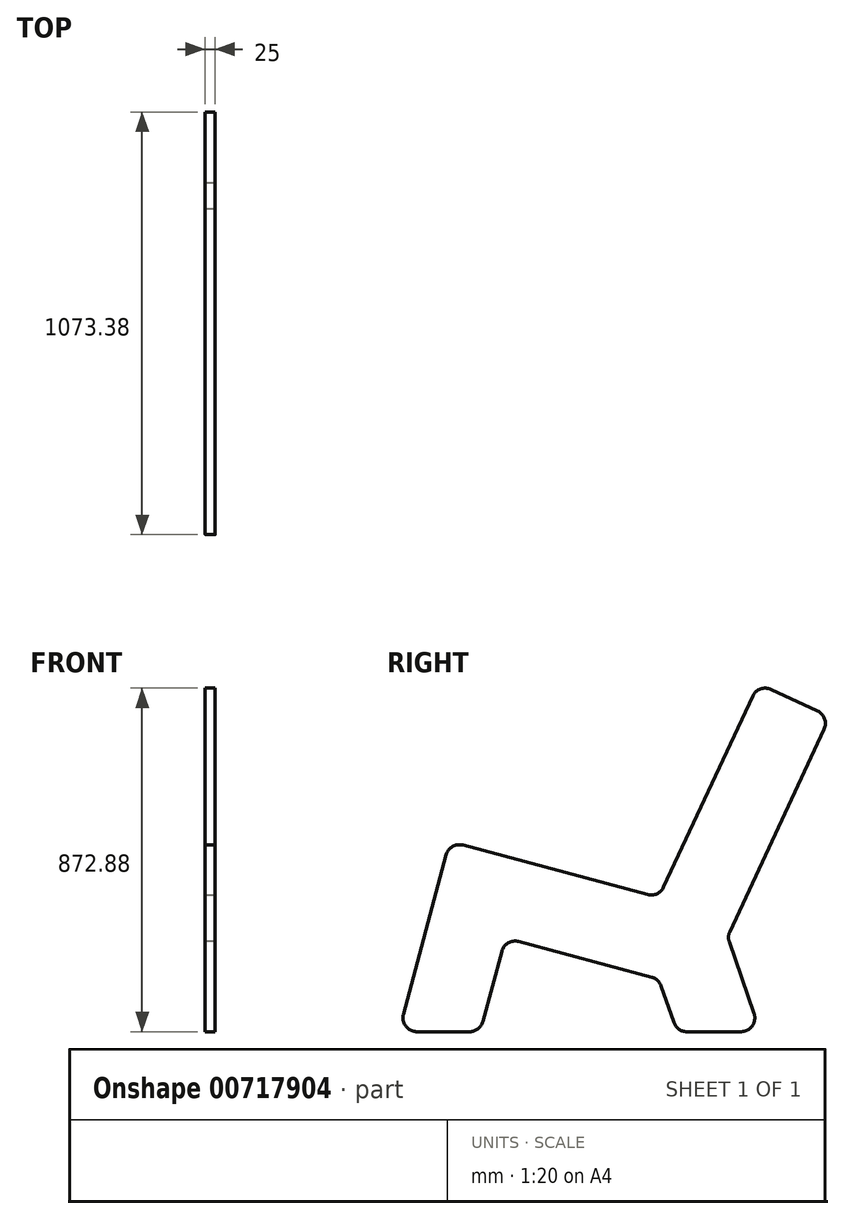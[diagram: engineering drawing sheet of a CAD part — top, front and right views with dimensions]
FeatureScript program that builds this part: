
annotation { "Feature Type Name" : "Feature", "Feature Type Description" : "" }
export const myFeature = defineFeature(function(context is Context, id is Id, definition is map)
    precondition{}
    {
        {
            var Q0;
            Q0=qCreatedBy(makeId("Right.planeOp"),FACE);
            cPlane(context, id + "F0", {"entities" : qUnion([Q0]), "cplaneType" : CPlaneType.OFFSET, "offset" : 400 * mm, "oppositeDirection" : true, "width" : 150 * mm, "height" : 150 * mm});
        }
        {
            var Q0;
            Q0=qCreatedBy(id+"F0.planeOp",FACE);
            var sketch = newSketch(context, id + "F1", { "sketchPlane" : qUnion([Q0])});
            skLineSegment(sketch, "E0", {"start": v(0, 0) * mm, "end": v(129.4, 482.96) * mm});
            skLineSegment(sketch, "E1", {"start": v(129.4, 482.96) * mm, "end": v(660.67, 340.61) * mm});
            skLineSegment(sketch, "E2", {"start": v(660.67, 340.61) * mm, "end": v(914.24, 884.4) * mm});
            skLineSegment(sketch, "E3", {"start": v(914.24, 884.4) * mm, "end": v(1095.5, 799.87) * mm});
            skLineSegment(sketch, "E4.0", {"start": v(207.06, 0) * mm, "end": v(270.83, 238.01) * mm});
            skLineSegment(sketch, "E5.0", {"start": v(270.83, 238.01) * mm, "end": v(660.67, 133.56) * mm});
            skLineSegment(sketch, "E6", {"start": v(0, 0) * mm, "end": v(207.06, 0) * mm});
            skLineSegment(sketch, "E7.0", {"start": v(835, 241.22) * mm, "end": v(1095.5, 799.87) * mm});
            skLineSegment(sketch, "E8", {"start": v(660.67, 133.56) * mm, "end": v(707.06, 0) * mm});
            skLineSegment(sketch, "E9.0", {"start": v(835, 241.22) * mm, "end": v(918.77, 0) * mm});
            skLineSegment(sketch, "E10", {"start": v(707.06, 0) * mm, "end": v(918.77, 0) * mm});
            skSolve(sketch);
        }
        {
            var Q0;
            Q0=makeQuery(id+"F1.imprint","IMPRINT",FACE,{"disambiguationData":[TD([[makeQuery(id+"F1.imprint","IMPRINT",EDGE,{"derivedFrom":sQuery(id+"F1.wireOp",EDGE,"E0")}),-1.0]])]});
            extrude(context, id + "F2", {"entities" : qUnion([Q0]), "depth" : 25 * mm, "offsetDistance" : 25 * mm});
        }
        {
            var Q0;
            Q0=makeQuery(id+"F2.opExtrude","SWEPT_EDGE",EDGE,{"disambiguationData":[OSD([sQuery(id+"F1.wireOp",EDGE,"E2"),sQuery(id+"F1.wireOp",EDGE,"E3")])]});
            var Q1;
            Q1=makeQuery(id+"F2.opExtrude","SWEPT_EDGE",EDGE,{"disambiguationData":[OSD([sQuery(id+"F1.wireOp",EDGE,"E3"),sQuery(id+"F1.wireOp",EDGE,"E7.0")])]});
            var Q2;
            Q2=makeQuery(id+"F2.opExtrude","SWEPT_EDGE",EDGE,{"disambiguationData":[OSD([sQuery(id+"F1.wireOp",EDGE,"E1"),sQuery(id+"F1.wireOp",EDGE,"E2")])]});
            var Q3;
            Q3=makeQuery(id+"F2.opExtrude","SWEPT_EDGE",EDGE,{"disambiguationData":[OSD([sQuery(id+"F1.wireOp",EDGE,"E0"),sQuery(id+"F1.wireOp",EDGE,"E1")])]});
            var Q4;
            Q4=makeQuery(id+"F2.opExtrude","SWEPT_EDGE",EDGE,{"disambiguationData":[OSD([sQuery(id+"F1.wireOp",EDGE,"E8"),sQuery(id+"F1.wireOp",EDGE,"E10")])]});
            var Q5;
            Q5=makeQuery(id+"F2.opExtrude","SWEPT_EDGE",EDGE,{"disambiguationData":[OSD([sQuery(id+"F1.wireOp",EDGE,"E0"),sQuery(id+"F1.wireOp",EDGE,"E6")])]});
            var Q6;
            Q6=makeQuery(id+"F2.opExtrude","SWEPT_EDGE",EDGE,{"disambiguationData":[OSD([sQuery(id+"F1.wireOp",EDGE,"E9.0"),sQuery(id+"F1.wireOp",EDGE,"E10")])]});
            var Q7;
            Q7=makeQuery(id+"F2.opExtrude","SWEPT_EDGE",EDGE,{"disambiguationData":[OSD([sQuery(id+"F1.wireOp",EDGE,"E4.0"),sQuery(id+"F1.wireOp",EDGE,"E6")])]});
            var Q8;
            Q8=makeQuery(id+"F2.opExtrude","SWEPT_EDGE",EDGE,{"disambiguationData":[OSD([sQuery(id+"F1.wireOp",EDGE,"E4.0"),sQuery(id+"F1.wireOp",EDGE,"E5.0")])]});
            var Q9;
            Q9=makeQuery(id+"F2.opExtrude","SWEPT_EDGE",EDGE,{"disambiguationData":[OSD([sQuery(id+"F1.wireOp",EDGE,"E5.0"),sQuery(id+"F1.wireOp",EDGE,"E8")])]});
            fillet(context, id + "F3", {"entities" : qUnion([Q0, Q1, Q2, Q3, Q4, Q5, Q6, Q7, Q8, Q9]), "radius" : 35 * mm, "tangentPropagation" : true, "allowEdgeOverflow" : false});
        }
        {
            var Q0;
            Q0=makeQuery(id+"F2.opExtrude","SWEPT_EDGE",EDGE,{"disambiguationData":[OSD([sQuery(id+"F1.wireOp",EDGE,"E7.0"),sQuery(id+"F1.wireOp",EDGE,"E9.0")])]});
            fillet(context, id + "F4", {"entities" : qUnion([Q0]), "radius" : 35 * mm, "tangentPropagation" : true, "allowEdgeOverflow" : false});
        }
    });
